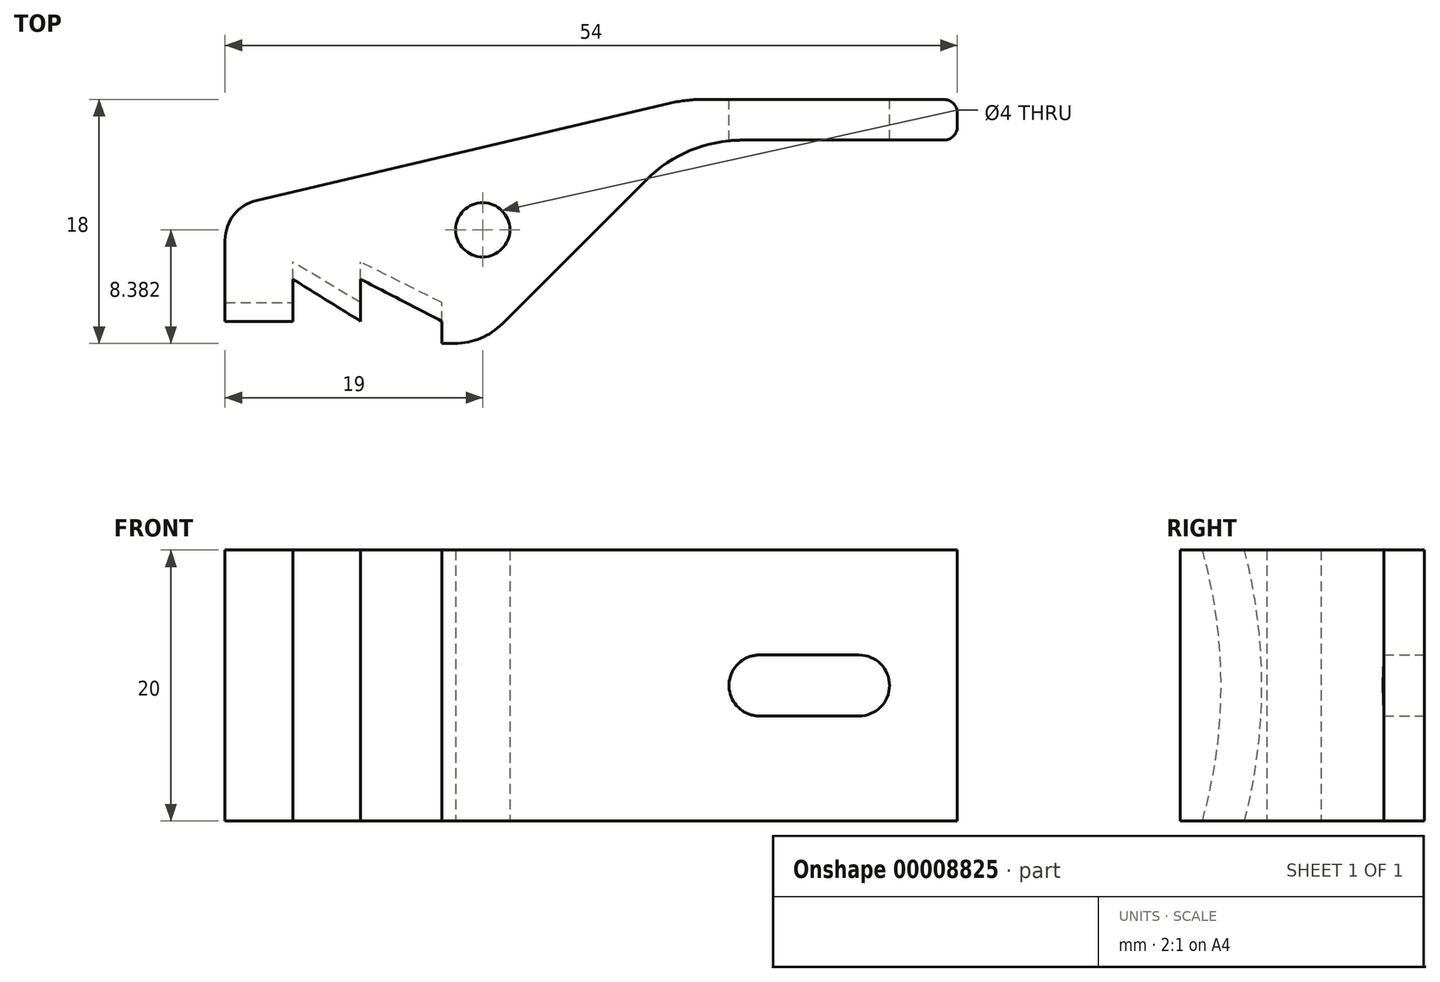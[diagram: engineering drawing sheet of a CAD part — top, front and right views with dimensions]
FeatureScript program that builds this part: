
annotation { "Feature Type Name" : "Feature", "Feature Type Description" : "" }
export const myFeature = defineFeature(function(context is Context, id is Id, definition is map)
    precondition{}
    {
        {
            var Q0;
            Q0=qCreatedBy(makeId("Top.planeOp"),FACE);
            var sketch = newSketch(context, id + "F0", { "sketchPlane" : qUnion([Q0])});
            skLineSegment(sketch, "E0", {"start": v(0, 0) * mm, "end": v(19, 0) * mm});
            skLineSegment(sketch, "E1", {"start": v(0, 0) * mm, "end": v(0, 10) * mm});
            skLineSegment(sketch, "E2", {"start": v(0, 10) * mm, "end": v(34, 18) * mm});
            skLineSegment(sketch, "E3", {"start": v(34, 18) * mm, "end": v(54, 18) * mm});
            skLineSegment(sketch, "E4", {"start": v(54, 18) * mm, "end": v(54, 15) * mm});
            skLineSegment(sketch, "E5", {"start": v(54, 15) * mm, "end": v(34, 15) * mm});
            skLineSegment(sketch, "E6", {"start": v(19, 0) * mm, "end": v(34, 15) * mm});
            skCircle(sketch, "E7", {"center": v(19, 8.38) * mm, "radius": 2 * mm});
            skLineSegment(sketch, "E8", {"start": v(19, 8.38) * mm, "end": v(23.2, 4.2) * mm, "construction": true});
            skLineSegment(sketch, "E9", {"start": v(19, 8.38) * mm, "end": v(17.64, 14.15) * mm, "construction": true});
            skSolve(sketch);
        }
        {
            var Q0;
            Q0=makeQuery(id+"F0.imprint","IMPRINT",FACE,{"disambiguationData":[TD([[makeQuery(id+"F0.imprint","IMPRINT",EDGE,{"derivedFrom":sQuery(id+"F0.wireOp",EDGE,"E0")}),1.0]])]});
            extrude(context, id + "F1", {"entities" : qUnion([Q0]), "endBound" : BoundingType.SYMMETRIC, "depth" : 20 * mm});
        }
        {
            var Q0;
            Q0=qCreatedBy(makeId("Top.planeOp"),FACE);
            var sketch = newSketch(context, id + "F2", { "sketchPlane" : qUnion([Q0])});
            skLineSegment(sketch, "E10.0", {"start": v(0, 0) * mm, "end": v(19, 0) * mm, "construction": true});
            skLineSegment(sketch, "E11", {"start": v(16, 0) * mm, "end": v(16, 3) * mm});
            skLineSegment(sketch, "E12", {"start": v(16, 3) * mm, "end": v(10, 6) * mm});
            skLineSegment(sketch, "E13", {"start": v(10, 6) * mm, "end": v(10, 3) * mm});
            skLineSegment(sketch, "E14", {"start": v(10, 3) * mm, "end": v(5, 6) * mm});
            skLineSegment(sketch, "E15", {"start": v(5, 6) * mm, "end": v(5, 3) * mm});
            skLineSegment(sketch, "E16", {"start": v(5, 3) * mm, "end": v(0, 3) * mm});
            skLineSegment(sketch, "E17", {"start": v(0, 3) * mm, "end": v(0, 0) * mm});
            skLineSegment(sketch, "E18", {"start": v(0, 3) * mm, "end": v(0, -10) * mm});
            skLineSegment(sketch, "E19", {"start": v(0, -10) * mm, "end": v(19, -10) * mm});
            skLineSegment(sketch, "E20", {"start": v(19, -10) * mm, "end": v(19, 0) * mm});
            skLineSegment(sketch, "E21", {"start": v(16, 0) * mm, "end": v(19, 0) * mm});
            skSolve(sketch);
        }
        {
            var Q0;
            Q0=qCreatedBy(makeId("Right.planeOp"),FACE);
            var sketch = newSketch(context, id + "F3", { "sketchPlane" : qUnion([Q0])});
            skCircle(sketch, "E22", {"center": v(-34, 0) * mm, "radius": 40 * mm});
            skSolve(sketch);
        }
        {
            var Q0;
            Q0=makeQuery(id+"F2.imprint","IMPRINT",FACE,{"disambiguationData":[TD([[makeQuery(id+"F2.imprint","IMPRINT",EDGE,{"derivedFrom":sQuery(id+"F2.wireOp",EDGE,"E11")}),1.0]])]});
            var Q1;
            Q1=sQuery(id+"F3.wireOp",EDGE,"E22");
            sweep(context, id + "F4", {"operationType" : NewBodyOperationType.REMOVE, "profiles" : qUnion([Q0]), "path" : qUnion([Q1])});
        }
        {
            var Q0;
            Q0=makeQuery(id+"F1.opExtrude","SWEPT_EDGE",EDGE,{"disambiguationData":[OSD([sQuery(id+"F0.wireOp",EDGE,"E1"),sQuery(id+"F0.wireOp",EDGE,"E2")])]});
            fillet(context, id + "F5", {"entities" : qUnion([Q0]), "radius" : 3 * mm, "tangentPropagation" : true, "allowEdgeOverflow" : false});
        }
        {
            var Q0;
            Q0=makeQuery(id+"F1.opExtrude","SWEPT_EDGE",EDGE,{"disambiguationData":[OSD([sQuery(id+"F0.wireOp",EDGE,"E5"),sQuery(id+"F0.wireOp",EDGE,"E6")])]});
            var Q1;
            Q1=makeQuery(id+"F1.opExtrude","SWEPT_EDGE",EDGE,{"disambiguationData":[OSD([sQuery(id+"F0.wireOp",EDGE,"E2"),sQuery(id+"F0.wireOp",EDGE,"E3")])]});
            fillet(context, id + "F6", {"entities" : qUnion([Q0, Q1]), "radius" : 10 * mm, "tangentPropagation" : true, "allowEdgeOverflow" : false});
        }
        {
            var Q0;
            Q0=makeQuery(id+"F1.opExtrude","SWEPT_EDGE",EDGE,{"disambiguationData":[OSD([sQuery(id+"F0.wireOp",EDGE,"E3"),sQuery(id+"F0.wireOp",EDGE,"E4")])]});
            var Q1;
            Q1=makeQuery(id+"F1.opExtrude","SWEPT_EDGE",EDGE,{"disambiguationData":[OSD([sQuery(id+"F0.wireOp",EDGE,"E4"),sQuery(id+"F0.wireOp",EDGE,"E5")])]});
            fillet(context, id + "F7", {"entities" : qUnion([Q0, Q1]), "radius" : 1 * mm, "tangentPropagation" : true, "allowEdgeOverflow" : false});
        }
        {
            var Q0;
            Q0=makeQuery(id+"F1.opExtrude","SWEPT_FACE",FACE,{"disambiguationData":[OSD([sQuery(id+"F0.wireOp",EDGE,"E3")])]});
            var sketch = newSketch(context, id + "F8", { "sketchPlane" : qUnion([Q0])});
            skLineSegment(sketch, "E23.rect.bottom", {"start": v(-39.41, -2.25) * mm, "end": v(-46.75, -2.25) * mm});
            skLineSegment(sketch, "E23.rect.top", {"start": v(-39.41, 2.25) * mm, "end": v(-46.75, 2.25) * mm});
            skLineSegment(sketch, "E23.rect.left", {"start": v(-39.41, -2.25) * mm, "end": v(-39.41, 2.25) * mm});
            skLineSegment(sketch, "E23.rect.right", {"start": v(-46.75, -2.25) * mm, "end": v(-46.75, 2.25) * mm});
            skPoint(sketch, "E23.rect.middle", {"position": v(-43.08, 0) * mm});
            skArc(sketch, "E24", {"start": v(-46.75, 2.25) * mm, "mid": v(-49, 0) * mm, "end": v(-46.75, -2.25) * mm});
            skArc(sketch, "E25", {"start": v(-39.41, -2.25) * mm, "mid": v(-37.16, 0) * mm, "end": v(-39.41, 2.25) * mm});
            skSolve(sketch);
        }
        {
            var Q0;
            Q0=makeQuery(id+"F8.imprint","IMPRINT",FACE,{"disambiguationData":[TD([[makeQuery(id+"F8.imprint","IMPRINT",EDGE,{"derivedFrom":sQuery(id+"F8.wireOp",EDGE,"E23.rect.bottom")}),-1.0]])]});
            var Q1;
            Q1=makeQuery(id+"F8.imprint","IMPRINT",FACE,{"disambiguationData":[TD([[makeQuery(id+"F8.imprint","IMPRINT",EDGE,{"derivedFrom":sQuery(id+"F8.wireOp",EDGE,"E23.rect.right")}),1.0]])]});
            var Q2;
            Q2=makeQuery(id+"F8.imprint","IMPRINT",FACE,{"disambiguationData":[TD([[makeQuery(id+"F8.imprint","IMPRINT",EDGE,{"derivedFrom":sQuery(id+"F8.wireOp",EDGE,"E23.rect.left")}),-1.0]])]});
            extrude(context, id + "F9", {"entities" : qUnion([Q0, Q1, Q2]), "operationType" : NewBodyOperationType.REMOVE, "endBound" : BoundingType.UP_TO_NEXT, "oppositeDirection" : true, "depth" : 25 * mm});
        }
        {
            var Q0;
            Q0=makeQuery(id+"F1.opExtrude","SWEPT_EDGE",EDGE,{"disambiguationData":[OSD([sQuery(id+"F0.wireOp",EDGE,"E0"),sQuery(id+"F0.wireOp",EDGE,"E6")])]});
            fillet(context, id + "F10", {"entities" : qUnion([Q0]), "radius" : 5 * mm, "tangentPropagation" : true, "allowEdgeOverflow" : false});
        }
    });
